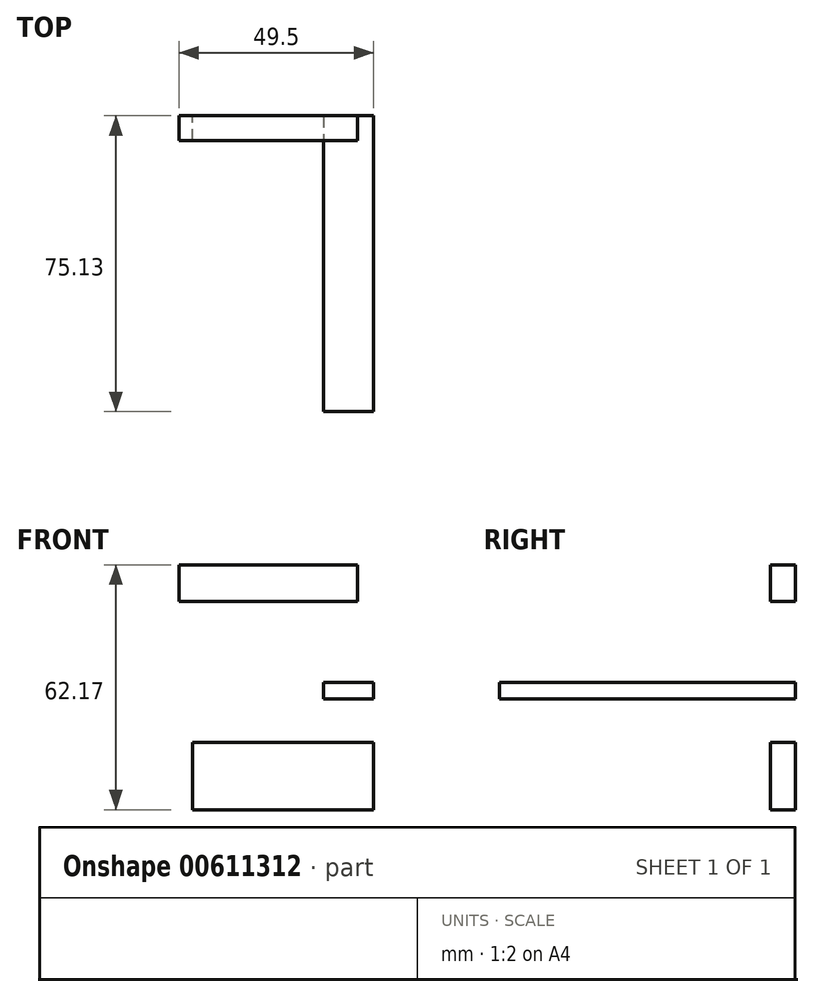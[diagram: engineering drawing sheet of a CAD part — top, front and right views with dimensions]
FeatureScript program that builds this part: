
annotation { "Feature Type Name" : "Feature", "Feature Type Description" : "" }
export const myFeature = defineFeature(function(context is Context, id is Id, definition is map)
    precondition{}
    {
        {
            var Q0;
            Q0=qCreatedBy(makeId("Front.planeOp"),FACE);
            var sketch = newSketch(context, id + "F0", { "sketchPlane" : qUnion([Q0])});
            skLineSegment(sketch, "E0.bottom", {"start": v(-75.9, 76.1) * mm, "end": v(0, 76.1) * mm});
            skLineSegment(sketch, "E0.top", {"start": v(-75.9, 0) * mm, "end": v(0, 0) * mm});
            skLineSegment(sketch, "E0.left", {"start": v(-75.9, 76.1) * mm, "end": v(-75.9, 0) * mm});
            skLineSegment(sketch, "E0.right", {"start": v(0, 76.1) * mm, "end": v(0, 0) * mm});
            skLineSegment(sketch, "E1.bottom", {"start": v(-67.24, 70.62) * mm, "end": v(-54.15, 70.62) * mm});
            skLineSegment(sketch, "E1.top", {"start": v(-67.24, 5.8) * mm, "end": v(-54.15, 5.8) * mm});
            skLineSegment(sketch, "E1.left", {"start": v(-67.24, 70.62) * mm, "end": v(-67.24, 5.8) * mm});
            skLineSegment(sketch, "E1.right", {"start": v(-54.15, 70.62) * mm, "end": v(-54.15, 5.8) * mm});
            skLineSegment(sketch, "E2", {"start": v(-67.24, 17) * mm, "end": v(-54.15, 17) * mm});
            skLineSegment(sketch, "E3.left", {"start": v(-52.04, 31.56) * mm, "end": v(-52.04, 31.77) * mm});
            skLineSegment(sketch, "E3.right", {"start": v(0, 31.56) * mm, "end": v(0, 31.77) * mm});
            skLineSegment(sketch, "E4.bottom", {"start": v(-49.5, 62.17) * mm, "end": v(-4.12, 62.17) * mm});
            skLineSegment(sketch, "E4.top", {"start": v(-49.5, 52.88) * mm, "end": v(-4.12, 52.88) * mm});
            skLineSegment(sketch, "E4.left", {"start": v(-49.5, 62.17) * mm, "end": v(-49.5, 52.88) * mm});
            skLineSegment(sketch, "E4.right", {"start": v(-4.12, 62.17) * mm, "end": v(-4.12, 52.88) * mm});
            skLineSegment(sketch, "E5.bottom", {"start": v(-52.04, 31.56) * mm, "end": v(0, 31.56) * mm});
            skLineSegment(sketch, "E5.top", {"start": v(-52.04, 31.77) * mm, "end": v(0, 31.77) * mm});
            skLineSegment(sketch, "E6.top", {"start": v(-52.04, 26.45) * mm, "end": v(0, 26.45) * mm});
            skLineSegment(sketch, "E6.left", {"start": v(-52.04, 31.56) * mm, "end": v(-52.04, 26.45) * mm});
            skLineSegment(sketch, "E6.right", {"start": v(0, 31.56) * mm, "end": v(0, 26.45) * mm});
            skLineSegment(sketch, "E7", {"start": v(-67.24, 27) * mm, "end": v(-52.04, 27) * mm});
            skLineSegment(sketch, "E8", {"start": v(-38.24, 62.17) * mm, "end": v(-38.24, 52.88) * mm});
            skLineSegment(sketch, "E9", {"start": v(-38.24, 52.88) * mm, "end": v(-26.81, 52.88) * mm});
            skLineSegment(sketch, "E10", {"start": v(-26.81, 52.88) * mm, "end": v(-26.81, 62.17) * mm});
            skLineSegment(sketch, "E11", {"start": v(-26.81, 62.17) * mm, "end": v(-15.48, 62.17) * mm});
            skLineSegment(sketch, "E12", {"start": v(-15.48, 62.17) * mm, "end": v(-15.48, 52.88) * mm});
            skLineSegment(sketch, "E13", {"start": v(-67.24, 27) * mm, "end": v(-67.24, 35.98) * mm});
            skLineSegment(sketch, "E14.0", {"start": v(-56.18, 70.62) * mm, "end": v(-56.18, 5.8) * mm});
            skLineSegment(sketch, "E15.0", {"start": v(-67.24, 68.58) * mm, "end": v(-54.15, 68.58) * mm});
            skLineSegment(sketch, "E16.0", {"start": v(-65.2, 70.62) * mm, "end": v(-65.2, 5.8) * mm});
            skLineSegment(sketch, "E17.0", {"start": v(-67.24, 7.84) * mm, "end": v(-54.15, 7.84) * mm});
            skSolve(sketch);
        }
        {
            var Q0;
            Q0=makeQuery(id+"F0.imprint","IMPRINT",FACE,{"disambiguationData":[TD([[makeQuery(id+"F0.imprint","IMPRINT",EDGE,{"derivedFrom":sQuery(id+"F0.wireOp",EDGE,"E4.bottom")}),-1.0]])]});
            extrude(context, id + "F1", {"entities" : qUnion([Q0]), "depth" : 6.35 * mm, "offsetDistance" : 25.4 * mm});
        }
        {
            var Q0;
            Q0=qCreatedBy(makeId("Right.planeOp"),FACE);
            var sketch = newSketch(context, id + "F2", { "sketchPlane" : qUnion([Q0])});
            skLineSegment(sketch, "E18.bottom", {"start": v(0, 28.18) * mm, "end": v(-75.13, 28.18) * mm});
            skLineSegment(sketch, "E18.top", {"start": v(0, 32.3) * mm, "end": v(-75.13, 32.3) * mm});
            skLineSegment(sketch, "E18.left", {"start": v(0, 28.18) * mm, "end": v(0, 32.3) * mm});
            skLineSegment(sketch, "E18.right", {"start": v(-75.13, 28.18) * mm, "end": v(-75.13, 32.3) * mm});
            skLineSegment(sketch, "E19.bottom", {"start": v(-16.67, 63.62) * mm, "end": v(-64.06, 63.62) * mm});
            skLineSegment(sketch, "E19.top", {"start": v(-16.67, 42.51) * mm, "end": v(-64.06, 42.51) * mm});
            skLineSegment(sketch, "E19.left", {"start": v(-16.67, 63.62) * mm, "end": v(-16.67, 42.51) * mm});
            skLineSegment(sketch, "E19.right", {"start": v(-64.06, 63.62) * mm, "end": v(-64.06, 42.51) * mm});
            skSolve(sketch);
        }
        {
            var Q0;
            Q0=makeQuery(id+"F2.imprint","IMPRINT",FACE,{"disambiguationData":[TD([[makeQuery(id+"F2.imprint","IMPRINT",EDGE,{"derivedFrom":sQuery(id+"F2.wireOp",EDGE,"E18.bottom")}),-1.0]])]});
            extrude(context, id + "F3", {"entities" : qUnion([Q0]), "oppositeDirection" : true, "depth" : 12.7 * mm, "offsetDistance" : 25.4 * mm});
        }
        {
            var Q0;
            Q0=sQuery(id+"F2.wireOp",EDGE,"E19.bottom");
            var Q1;
            Q1=sQuery(id+"F2.wireOp",EDGE,"E19.right");
            var Q2;
            Q2=sQuery(id+"F2.wireOp",EDGE,"E19.top");
            var Q3;
            Q3=sQuery(id+"F2.wireOp",EDGE,"E19.left");
            extrude(context, id + "F4", {"bodyType" : ToolBodyType.SURFACE, "surfaceEntities" : qUnion([Q0, Q1, Q2, Q3]), "oppositeDirection" : true, "depth" : 2.54 * mm, "offsetDistance" : 25.4 * mm});
        }
        {
            var Q0;
            Q0=qCreatedBy(makeId("Front.planeOp"),FACE);
            var sketch = newSketch(context, id + "F5", { "sketchPlane" : qUnion([Q0])});
            skLineSegment(sketch, "E20.bottom", {"start": v(0, 17.1) * mm, "end": v(-46.04, 17.1) * mm});
            skLineSegment(sketch, "E20.top", {"start": v(0, 0) * mm, "end": v(-46.04, 0) * mm});
            skLineSegment(sketch, "E20.left", {"start": v(0, 17.1) * mm, "end": v(0, 0) * mm});
            skLineSegment(sketch, "E20.right", {"start": v(-46.04, 17.1) * mm, "end": v(-46.04, 0) * mm});
            skSolve(sketch);
        }
        {
            var Q0;
            Q0 = qSketchRegion(id + "F5", true);
            extrude(context, id + "F6", {"entities" : qUnion([Q0]), "depth" : 6.35 * mm, "offsetDistance" : 25.4 * mm});
        }
    });
